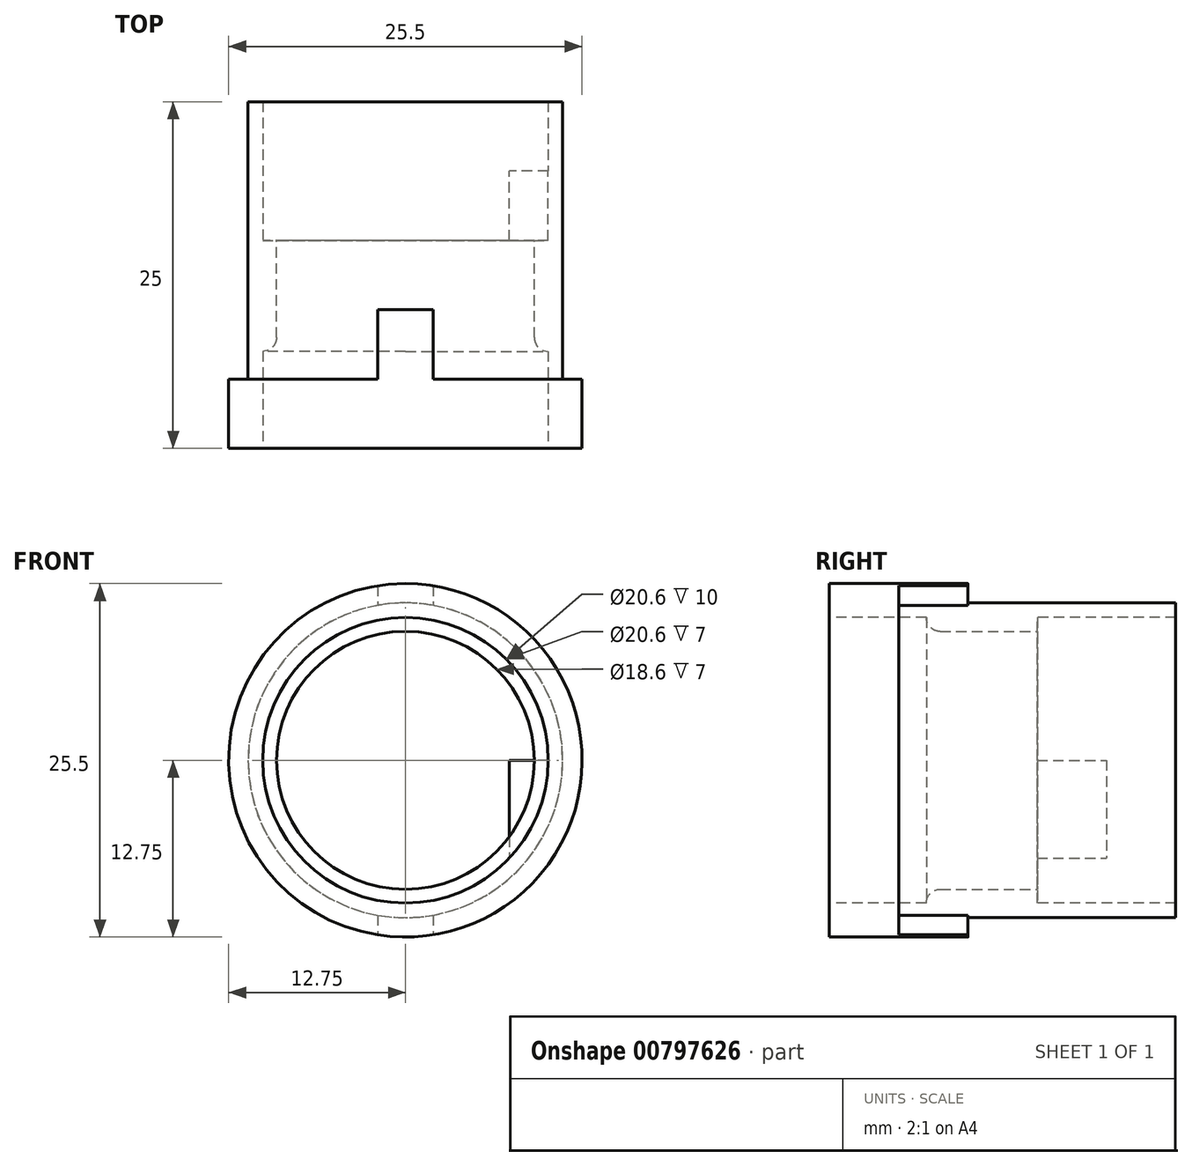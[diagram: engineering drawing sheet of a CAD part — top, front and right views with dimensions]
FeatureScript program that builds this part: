
annotation { "Feature Type Name" : "Feature", "Feature Type Description" : "" }
export const myFeature = defineFeature(function(context is Context, id is Id, definition is map)
    precondition{}
    {
        {
            var Q0;
            Q0=qCreatedBy(makeId("Front.planeOp"),FACE);
            var sketch = newSketch(context, id + "F0", { "sketchPlane" : qUnion([Q0])});
            skCircle(sketch, "E0", {"center": v(0, 0) * mm, "radius": 10.3 * mm});
            skSolve(sketch);
        }
        {
            var Q0;
            Q0=makeQuery(id+"F0.imprint","IMPRINT",FACE,{"disambiguationData":[TD([[makeQuery(id+"F0.imprint","IMPRINT",EDGE,{"derivedFrom":sQuery(id+"F0.wireOp",EDGE,"E0")}),1.0]])]});
            extrude(context, id + "F1", {"entities" : qUnion([Q0]), "depth" : 9 * mm, "offsetDistance" : 25 * mm});
        }
        {
            var Q0;
            Q0=makeQuery(id+"F1.opExtrude","CAP_FACE",FACE,{"disambiguationData":[OSD([sQuery(id+"F0.wireOp",EDGE,"E0")])],"isStart":true});
            var sketch = newSketch(context, id + "F2", { "sketchPlane" : qUnion([Q0])});
            skCircle(sketch, "E1", {"center": v(0, 0) * mm, "radius": 9.25 * mm});
            skCircle(sketch, "E2", {"center": v(0, 0) * mm, "radius": 11.25 * mm});
            skSolve(sketch);
        }
        {
            var Q0;
            Q0=makeQuery(id+"F1.opExtrude","CAP_FACE",FACE,{"disambiguationData":[OSD([sQuery(id+"F0.wireOp",EDGE,"E0")])],"isStart":false});
            var sketch = newSketch(context, id + "F3", { "sketchPlane" : qUnion([Q0])});
            skCircle(sketch, "E3", {"center": v(0, 0) * mm, "radius": 3.1 * mm});
            skSolve(sketch);
        }
        {
            var Q0;
            Q0=makeQuery(id+"F3.imprint","IMPRINT",FACE,{"disambiguationData":[TD([[makeQuery(id+"F3.imprint","IMPRINT",EDGE,{"derivedFrom":sQuery(id+"F3.wireOp",EDGE,"E3")}),1.0]])]});
            extrude(context, id + "F4", {"entities" : qUnion([Q0]), "operationType" : NewBodyOperationType.REMOVE, "endBound" : BoundingType.THROUGH_ALL, "oppositeDirection" : true, "depth" : 25 * mm, "offsetDistance" : 25 * mm});
        }
        {
            var Q0;
            Q0=makeQuery(id+"F1.opExtrude","CAP_FACE",FACE,{"disambiguationData":[OSD([sQuery(id+"F0.wireOp",EDGE,"E0")])],"isStart":false});
            var sketch = newSketch(context, id + "F5", { "sketchPlane" : qUnion([Q0])});
            skCircle(sketch, "E4", {"center": v(-4.33, 2.5) * mm, "radius": 2.5 * mm});
            skCircle(sketch, "E5", {"center": v(4.33, 2.5) * mm, "radius": 2.5 * mm});
            skCircle(sketch, "E6", {"center": v(0, -5) * mm, "radius": 2.5 * mm});
            skSolve(sketch);
        }
        {
            var Q0;
            {var subQ0=sQuery(id+"F5.wireOp",EDGE,"E4");var subQ1=makeQuery(id+"F4.boolean.opBoolean","COPY",EDGE,{"derivedFrom":makeQuery(id+"F4.opExtrude","CAP_EDGE",EDGE,{"disambiguationData":[OSD([sQuery(id+"F3.wireOp",EDGE,"E3")])],"isStart":true})});var subQ2=makeQuery(id+"F5.imprint","INTERSECT",VERTEX,{"disambiguationData":[OD(0.0)],"derivedFrom":[subQ1,subQ0]});Q0=makeQuery(id+"F5.imprint","IMPRINT",FACE,{"disambiguationData":[TD([[makeQuery(id+"F5.imprint","IMPRINT",EDGE,{"disambiguationData":[TD([[subQ2,1.0]])],"derivedFrom":subQ0}),1.0]])]});}
            var Q1;
            {var subQ0=sQuery(id+"F5.wireOp",EDGE,"E5");var subQ1=makeQuery(id+"F4.boolean.opBoolean","COPY",EDGE,{"derivedFrom":makeQuery(id+"F4.opExtrude","CAP_EDGE",EDGE,{"disambiguationData":[OSD([sQuery(id+"F3.wireOp",EDGE,"E3")])],"isStart":true})});var subQ2=makeQuery(id+"F5.imprint","INTERSECT",VERTEX,{"disambiguationData":[OD(0.0)],"derivedFrom":[subQ1,subQ0]});Q1=makeQuery(id+"F5.imprint","IMPRINT",FACE,{"disambiguationData":[TD([[makeQuery(id+"F5.imprint","IMPRINT",EDGE,{"disambiguationData":[TD([[subQ2,1.0]])],"derivedFrom":subQ0}),1.0]])]});}
            var Q2;
            {var subQ0=sQuery(id+"F5.wireOp",EDGE,"E6");var subQ1=makeQuery(id+"F4.boolean.opBoolean","COPY",EDGE,{"derivedFrom":makeQuery(id+"F4.opExtrude","CAP_EDGE",EDGE,{"disambiguationData":[OSD([sQuery(id+"F3.wireOp",EDGE,"E3")])],"isStart":true})});var subQ2=makeQuery(id+"F5.imprint","INTERSECT",VERTEX,{"disambiguationData":[OD(0.0)],"derivedFrom":[subQ1,subQ0]});Q2=makeQuery(id+"F5.imprint","IMPRINT",FACE,{"disambiguationData":[TD([[makeQuery(id+"F5.imprint","IMPRINT",EDGE,{"disambiguationData":[TD([[subQ2,-1.0]])],"derivedFrom":subQ0}),1.0]])]});}
            extrude(context, id + "F6", {"entities" : qUnion([Q0, Q1, Q2]), "operationType" : NewBodyOperationType.REMOVE, "oppositeDirection" : true, "depth" : 1.8 * mm, "offsetDistance" : 25 * mm});
        }
        {
            var Q0;
            Q0=makeQuery(id+"F6.boolean.opBoolean","COPY",EDGE,{"derivedFrom":makeQuery(id+"F6.opExtrude","CAP_EDGE",EDGE,{"disambiguationData":[OSD([sQuery(id+"F5.wireOp",EDGE,"E4")])],"isStart":false})});
            var Q1;
            Q1=makeQuery(id+"F6.boolean.opBoolean","COPY",EDGE,{"derivedFrom":makeQuery(id+"F6.opExtrude","CAP_EDGE",EDGE,{"disambiguationData":[OSD([sQuery(id+"F5.wireOp",EDGE,"E5")])],"isStart":false})});
            var Q2;
            Q2=makeQuery(id+"F6.boolean.opBoolean","COPY",EDGE,{"derivedFrom":makeQuery(id+"F6.opExtrude","CAP_EDGE",EDGE,{"disambiguationData":[OSD([sQuery(id+"F5.wireOp",EDGE,"E6")])],"isStart":false})});
            fillet(context, id + "F7", {"entities" : qUnion([Q0, Q1, Q2]), "radius" : 1 * mm, "tangentPropagation" : true, "allowEdgeOverflow" : false});
        }
        {
            var Q0;
            Q0=makeQuery(id+"F2.imprint","IMPRINT",FACE,{"disambiguationData":[TD([[makeQuery(id+"F2.imprint","IMPRINT",EDGE,{"derivedFrom":sQuery(id+"F2.wireOp",EDGE,"E1")}),1.0]])]});
            cPlane(context, id + "F8", {"entities" : qUnion([Q0]), "cplaneType" : CPlaneType.OFFSET, "offset" : 0 * mm, "width" : 150 * mm, "height" : 150 * mm});
        }
        {
            var Q0;
            Q0=qCreatedBy(id+"F8.planeOp",FACE);
            var sketch = newSketch(context, id + "F9", { "sketchPlane" : qUnion([Q0])});
            skCircle(sketch, "E7", {"center": v(0, 0) * mm, "radius": 12.75 * mm});
            skSolve(sketch);
        }
        {
            var Q0;
            Q0=qSketchRegion(id+"F9",true);
            extrude(context, id + "F10", {"entities" : qUnion([Q0]), "operationType" : NewBodyOperationType.ADD, "depth" : 25 * mm, "offsetDistance" : 25 * mm});
        }
        {
            var Q0;
            Q0=makeQuery(id+"F10.opExtrude","CAP_FACE",FACE,{"disambiguationData":[OSD([sQuery(id+"F9.wireOp",EDGE,"E7")])],"isStart":false});
            var sketch = newSketch(context, id + "F11", { "sketchPlane" : qUnion([Q0])});
            skCircle(sketch, "E8", {"center": v(0, 0) * mm, "radius": 3.1 * mm});
            skSolve(sketch);
        }
        {
            var Q0;
            Q0=makeQuery(id+"F11.imprint","IMPRINT",FACE,{"disambiguationData":[TD([[makeQuery(id+"F11.imprint","IMPRINT",EDGE,{"derivedFrom":sQuery(id+"F11.wireOp",EDGE,"E8")}),1.0]])]});
            extrude(context, id + "F12", {"entities" : qUnion([Q0]), "operationType" : NewBodyOperationType.REMOVE, "endBound" : BoundingType.THROUGH_ALL, "oppositeDirection" : true, "depth" : 25 * mm, "offsetDistance" : 25 * mm});
        }
        {
            var Q0;
            Q0=makeQuery(id+"F10.opExtrude","CAP_FACE",FACE,{"disambiguationData":[OSD([sQuery(id+"F9.wireOp",EDGE,"E7")])],"isStart":false});
            var sketch = newSketch(context, id + "F13", { "sketchPlane" : qUnion([Q0])});
            skCircle(sketch, "E9", {"center": v(0, 0) * mm, "radius": 11.35 * mm});
            skSolve(sketch);
        }
        {
            var Q0;
            Q0=makeQuery(id+"F13.imprint","IMPRINT",FACE,{"disambiguationData":[TD([[makeQuery(id+"F13.imprint","IMPRINT",EDGE,{"derivedFrom":sQuery(id+"F13.wireOp",EDGE,"E9")}),-1.0]])]});
            extrude(context, id + "F14", {"entities" : qUnion([Q0]), "operationType" : NewBodyOperationType.REMOVE, "oppositeDirection" : true, "depth" : 20 * mm, "offsetDistance" : 25 * mm});
        }
        {
            var Q0;
            Q0=makeQuery(id+"F14.boolean.opBoolean","COPY",FACE,{"derivedFrom":makeQuery(id+"F14.opExtrude","CAP_FACE",FACE,{"disambiguationData":[OSD([sQuery(id+"F9.wireOp",EDGE,"E7"),sQuery(id+"F13.wireOp",EDGE,"E9")])],"isStart":false})});
            var sketch = newSketch(context, id + "F15", { "sketchPlane" : qUnion([Q0])});
            skLineSegment(sketch, "E10", {"start": v(0, 13.66) * mm, "end": v(0, -14.8) * mm, "construction": true});
            skLineSegment(sketch, "E11", {"start": v(-2, 12.6) * mm, "end": v(-2, 11.17) * mm});
            skLineSegment(sketch, "E12", {"start": v(2, 12.6) * mm, "end": v(2, 11.17) * mm});
            skLineSegment(sketch, "E13", {"start": v(-14.5, 0) * mm, "end": v(13.95, 0) * mm, "construction": true});
            skLineSegment(sketch, "E14.MirrorCS", {"start": v(-6, 12.6) * mm, "end": v(-6, 11.17) * mm});
            skLineSegment(sketch, "E15.MirrorCS", {"start": v(10.5, 0) * mm, "end": v(-17.95, 0) * mm, "construction": true});
            skLineSegment(sketch, "E16", {"start": v(-2, -11.17) * mm, "end": v(-2, -12.6) * mm});
            skLineSegment(sketch, "E17", {"start": v(2, -11.17) * mm, "end": v(2, -12.6) * mm});
            skPoint(sketch, "E18.MirrorCS.end.orphan", {"position": v(-6, 11.17) * mm});
            skPoint(sketch, "E18.MirrorCS.start.orphan", {"position": v(-6, 12.6) * mm});
            skSolve(sketch);
        }
        {
            var Q0;
            {var subQ0=sQuery(id+"F15.wireOp",EDGE,"E11");Q0=makeQuery(id+"F15.imprint","IMPRINT",FACE,{"disambiguationData":[TD([[makeQuery(id+"F15.imprint","IMPRINT",EDGE,{"derivedFrom":subQ0}),1.0]])]});}
            var Q1;
            {var subQ0=sQuery(id+"F15.wireOp",EDGE,"E16");Q1=makeQuery(id+"F15.imprint","IMPRINT",FACE,{"disambiguationData":[TD([[makeQuery(id+"F15.imprint","IMPRINT",EDGE,{"derivedFrom":subQ0}),1.0]])]});}
            extrude(context, id + "F16", {"entities" : qUnion([Q0, Q1]), "operationType" : NewBodyOperationType.ADD, "depth" : 5 * mm, "offsetDistance" : 25 * mm});
        }
        {
            var Q0;
            Q0=makeQuery(id+"F1.opExtrude","CAP_FACE",FACE,{"disambiguationData":[OSD([sQuery(id+"F0.wireOp",EDGE,"E0")])],"isStart":false});
            var sketch = newSketch(context, id + "F17", { "sketchPlane" : qUnion([Q0])});
            skCircle(sketch, "E19", {"center": v(0, 0) * mm, "radius": 10.3 * mm});
            skSolve(sketch);
        }
        {
            var Q0;
            Q0 = qSketchRegion(id + "F17", true);
            extrude(context, id + "F18", {"entities" : qUnion([Q0]), "operationType" : NewBodyOperationType.REMOVE, "endBound" : BoundingType.THROUGH_ALL, "oppositeDirection" : true, "depth" : 25 * mm, "offsetDistance" : 25 * mm});
        }
        {
            var Q0;
            Q0=makeQuery(id+"F10.opExtrude","CAP_FACE",FACE,{"disambiguationData":[OSD([sQuery(id+"F9.wireOp",EDGE,"E7")])],"isStart":false});
            var sketch = newSketch(context, id + "F19", { "sketchPlane" : qUnion([Q0])});
            skLineSegment(sketch, "E20", {"start": v(-10.3, 0) * mm, "end": v(-7.5, 0) * mm});
            skLineSegment(sketch, "E21", {"start": v(-7.5, 0) * mm, "end": v(-7.5, -7.06) * mm});
            skSolve(sketch);
        }
        {
            var Q0;
            {var subQ0=sQuery(id+"F19.wireOp",EDGE,"E20");Q0=makeQuery(id+"F19.imprint","IMPRINT",FACE,{"disambiguationData":[TD([[makeQuery(id+"F19.imprint","IMPRINT",EDGE,{"derivedFrom":subQ0}),-1.0]])]});}
            extrude(context, id + "F20", {"entities" : qUnion([Q0]), "operationType" : NewBodyOperationType.ADD, "oppositeDirection" : true, "depth" : 10 * mm, "offsetDistance" : 25 * mm, "hasSecondDirection" : true, "secondDirectionOppositeDirection" : true, "secondDirectionDepth" : 5 * mm});
        }
        {
            var Q0;
            Q0=makeQuery(id+"F20.opExtrude","CAP_FACE",FACE,{"disambiguationData":[OSD([sQuery(id+"F9.wireOp",EDGE,"E7"),sQuery(id+"F17.wireOp",EDGE,"E19"),sQuery(id+"F19.wireOp",EDGE,"E20"),sQuery(id+"F19.wireOp",EDGE,"E21")])],"isStart":false});
            var sketch = newSketch(context, id + "F21", { "sketchPlane" : qUnion([Q0])});
            skCircle(sketch, "E22", {"center": v(0, 0) * mm, "radius": 9.3 * mm});
            skCircle(sketch, "E23", {"center": v(0, 0) * mm, "radius": 10.3 * mm});
            skSolve(sketch);
        }
        {
            var Q0;
            Q0 = qSketchRegion(id + "F21", true);
            extrude(context, id + "F22", {"entities" : qUnion([Q0]), "operationType" : NewBodyOperationType.ADD, "depth" : 8 * mm, "offsetDistance" : 25 * mm});
        }
        {
            var Q0;
            Q0=makeQuery(id+"F22.opExtrude","CAP_EDGE",EDGE,{"disambiguationData":[OSD([sQuery(id+"F21.wireOp",EDGE,"E22")])],"isStart":false});
            fillet(context, id + "F23", {"entities" : qUnion([Q0]), "tangentPropagation" : true, "radius" : 1 * mm, "defaultsChanged" : true, "vertexSettings" : [], "allowEdgeOverflow" : false});
        }
    });
